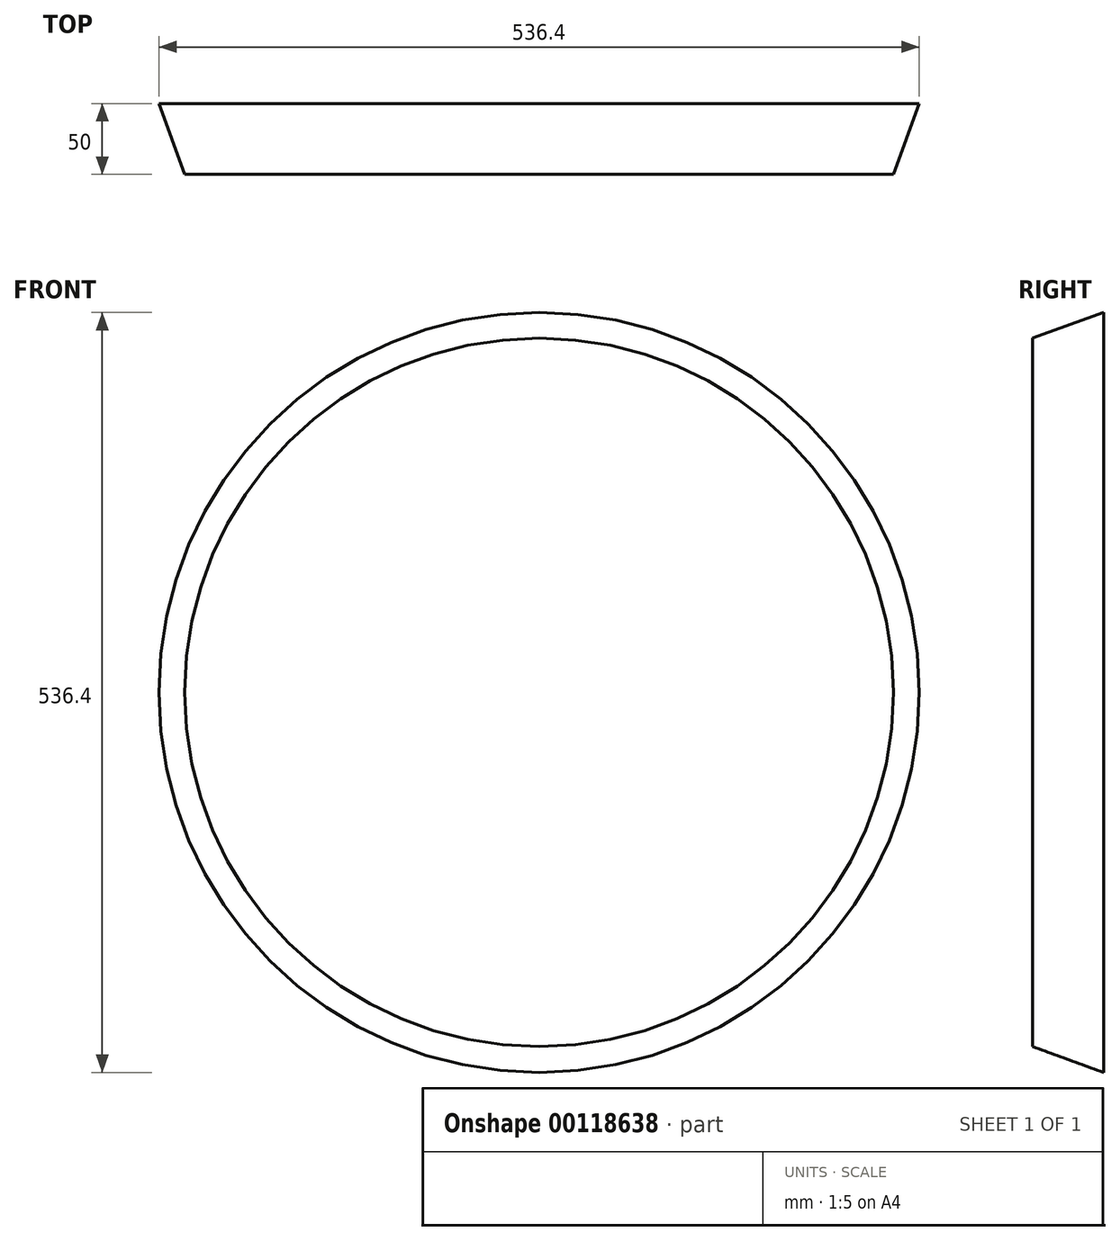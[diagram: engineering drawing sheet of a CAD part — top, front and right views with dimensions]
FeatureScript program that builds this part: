
annotation { "Feature Type Name" : "Feature", "Feature Type Description" : "" }
export const myFeature = defineFeature(function(context is Context, id is Id, definition is map)
    precondition{}
    {
        {
            var Q0;
            Q0=qCreatedBy(makeId("Front.planeOp"),FACE);
            var sketch = newSketch(context, id + "F0", { "sketchPlane" : qUnion([Q0])});
            skCircle(sketch, "E0", {"center": v(0, 0) * mm, "radius": 300 * mm});
            skSolve(sketch);
        }
        {
            var Q0;
            Q0 = qSketchRegion(id + "F0", true);
            extrude(context, id + "F1", {"entities" : qUnion([Q0]), "depth" : 50 * mm});
        }
        {
            var Q0;
            Q0=makeQuery(id+"F1.opExtrude","CAP_EDGE",EDGE,{"disambiguationData":[OSD([sQuery(id+"F0.wireOp",EDGE,"E0")])],"isStart":false});
            chamfer(context, id + "F2", {"entities" : qUnion([Q0]), "chamferType" : ChamferType.OFFSET_ANGLE, "width" : 50 * mm, "oppositeDirection" : false, "angle" : 70 * degree, "tangentPropagation" : true});
        }
    });
